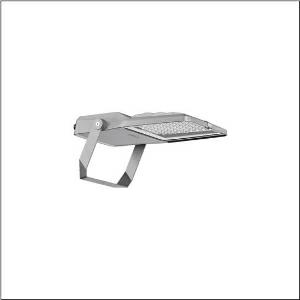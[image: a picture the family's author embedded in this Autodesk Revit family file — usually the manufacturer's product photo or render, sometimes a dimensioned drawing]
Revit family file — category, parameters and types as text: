
# Revit family: floodlight_fl_21_mini___pl52_5xa7772c5d1a_21b2
name_source: partatom
category: Lighting Fixtures
units: mm (PartAtom-declared; Revit-internal decimal feet)

## family parameters
Cut with Voids When Loaded = No
Host = Face
Light Source = No
Part Type = Normal
Room Calculation Point = No
Round Connector Dimension = Use Diameter
Shared = No

## types (1)
- --- (1 x LED, 11390 lm, 87.2 W, 4000K)
    Apparent Load = 87 VA
    CIE Flux Codes = 26 60 98 100 100
    Color Rendering = 80
    Color Temperature = 4000K
    Default Elevation = 1800 mm
    Description = Floodlight FL 21 mini, floodlight, primary light control with lens, of PMMA, primary optical cover: protective disc, of toughened safety glass, transparent, light distribution: PL52, light emission: direct distribution, installation type: surface-mounted, LED, High Power LED, rated luminous flux: 11.390lm, luminous efficacy: 131lm/W, light colour: 840, colour temperature: 4000K, control gear: ECG iQ, control: Street-Remote, Auto-Match, Temp-Guard, Night-Set, Smart-Wire, Desk-Remote (wireless, voltage-free reading and setting of iQ features in the workshop via application-optimized NFC function/RFID function), optimised constant luminous flux control (CLO 2.0), with terminal, 6-pole, mains connection: 220..240V, AC, 50/60Hz, start of lifetime: 87W, end of lifetime: 92W, reduction: 40W, luminaire housing, of diecast aluminium, powder-coated, Siteco® metallic grey (DB 702S), corrosivity category C5 according to DIN EN ISO 12944, mounting bracket, of steel, galvanised, powder-coated, Siteco® metallic grey (DB 702S), protection rating (complete): IP66, insulation class (complete): insulation class II (safety insulation), certification: CE, ENEC, VDE, protection symbol: D, impact resistance: IK08, permissible operating ambient temperature: -40..+40°C, permissible operating ambient temperature for outdoor applications: -40..+50°C, standard: DIN EN 12944, packaging unit: 1 piece

Light Distribution: PL52
    Height = 70 mm
    Lamp = 1 x LED
    Lamp Light Flux = 11390 lm
    Lamp Power = 87.2 W
    Lamp count = 1
    Length = 485 mm
    Luminous efficacy = 131 lm/W
    Manufacturer = Siteco
    ModVariant = No
    Model = 5XA7772C5D1A
    Number of Poles = 1
    OnlyDefault = Yes
    Power Factor = 1
    Product Name = Floodlight FL 21 mini | PL52
    Product group = floodlight | pylon top
    ProductGroupID = 6101
    Protection Class = Protection class II
    Protection Degree = IP 66
    RLX_Detail_Level = 1
    RlxData = <blob elided: 96341 chars, md5=48cadd77>
    Socket = socket
    Standby Power = 0 W
    System Light Flux = 11390 lm
    System Power = 87 W
    Type Comments = factory setting: luminous flux: 100 % | dim-lin: 254 | 456 mA
    Type Image = l_1006845.jpg
    URL = http://relux.com
    VarID = @adj_075243
    Voltage = 0 V
    Weight = 0.00 kg
    Width = 337 mm

## geometry (parser evidence)
native form markers: Blend x4, Sweep x12
no freeform markers — native parametric forms only
